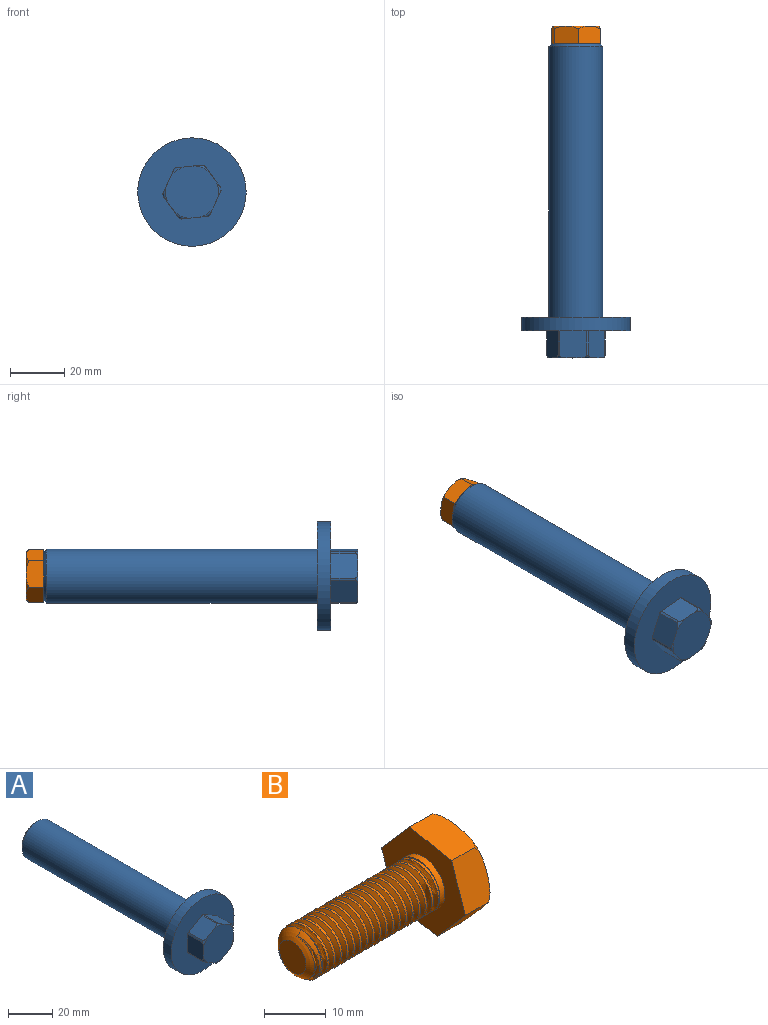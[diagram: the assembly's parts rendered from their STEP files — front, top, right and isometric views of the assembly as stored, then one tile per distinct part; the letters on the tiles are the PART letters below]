
ASSEMBLY  parts=2 mates=1
PART A: 31 faces, bbox 40x116.6x40 mm
  f0: cylinder r=4.25mm len=34.98mm, axis (0,-1,0), area 369.2mm2, adj f2,f3,f15,f29,f30
  f1: plane 17.97x17.97mm, normal (0,1,0), area 174.4mm2, adj f2,f3,f22,f30
  f2: bspline ~35.78x11.94mm, area 726mm2, adj f0,f1,f3,f29,f30
  f3: bspline ~36.03x11.94mm, area 738.2mm2, adj f0,f1,f2,f29,f30
  f4: cylinder r=10.75mm len=9mm, axis (0,-1,0), area 7.1mm2, adj f5,f19,f23,f28
  f5: torus R=9.75mm, axis (0,-1,0), area 3.7mm2, adj f4,f21,f23,f28
  f6: torus R=9.75mm, axis (0,-1,0), area 3.7mm2, adj f12,f21,f24,f28
  f7: cylinder r=10.75mm len=9mm, axis (0,-1,0), area 7.1mm2, adj f8,f19,f24,f27
  f8: torus R=9.75mm, axis (0,-1,0), area 3.7mm2, adj f7,f21,f24,f27
  f9: torus R=9.75mm, axis (0,-1,0), area 3.7mm2, adj f11,f21,f25,f27
  f10: cylinder r=10.75mm len=9mm, axis (0,-1,0), area 7.1mm2, adj f13,f19,f23,f26
  f11: cylinder r=10.75mm len=9mm, axis (0,-1,0), area 7.1mm2, adj f9,f19,f25,f27
  f12: cylinder r=10.75mm len=9mm, axis (0,-1,0), area 7.1mm2, adj f6,f19,f24,f28
  f13: torus R=9.75mm, axis (0,-1,0), area 3.7mm2, adj f10,f21,f23,f26
  f14: torus R=9.75mm, axis (0,-1,0), area 3.7mm2, adj f20,f21,f25,f26
  f15: cone r=4.25mm half-angle=45deg, axis (0,1,0), area 80.2mm2, adj f0
  f16: cylinder r=9.97mm len=100mm, axis (0,-1,0), area 6267.5mm2, adj f17,f22
  f17: plane 40x40mm, normal (0,1,0), area 944mm2, adj f16,f18
  f18: cylinder r=20mm len=40mm, axis (0,-1,0), area 628.3mm2, adj f17,f19
  f19: plane 40x40mm, normal (0,-1,0), area 944.5mm2, adj f4,f7,f10,f11,f12,f18,f20,f23
  f20: cylinder r=10.75mm len=9mm, axis (0,-1,0), area 7.1mm2, adj f14,f19,f25,f26
  f21: plane 19.5x19mm, normal (0,-1,0), area 294.2mm2, adj f5,f6,f8,f9,f13,f14,f23,f24
  f22: cone r=9.97mm half-angle=45deg, axis (0,-1,0), area 84.2mm2, adj f1,f16
  f23: plane 10x8.71mm, normal (0.5,0,0.87), area 99.6mm2, adj f4,f5,f10,f13,f19,f21
  f24: plane 10.06x10mm, normal (-1,0,0), area 99.6mm2, adj f6,f7,f8,f12,f19,f21
  f25: plane 10x8.71mm, normal (0.5,0,-0.87), area 99.6mm2, adj f9,f11,f14,f19,f20,f21
  f26: plane 10.06x10mm, normal (1,0,0), area 99.6mm2, adj f10,f13,f14,f19,f20,f21
  f27: plane 10x8.71mm, normal (-0.5,0,-0.87), area 99.6mm2, adj f7,f8,f9,f11,f19,f21
  f28: plane 10x8.71mm, normal (-0.5,0,0.87), area 99.6mm2, adj f4,f5,f6,f12,f19,f21
  f29: plane 1.06x0.8mm, normal (-0.87,0,-0.5), area 0.5mm2, adj f0,f2,f3
  f30: cone r=5.69mm half-angle=44.1deg, axis (0,1,0), area 18.1mm2, adj f0,f1,f2,f3
PART B: 17 faces, bbox 37.1x20.2x20.2 mm
  f0: plane 7.39x6.5mm, normal (0,0.75,0.66), area 60.9mm2, adj f1,f5,f6,f15
  f1: plane 9.63x6.5mm, normal (0,-0.19,0.98), area 60.9mm2, adj f0,f2,f6,f15
  f2: plane 9.29x6.5mm, normal (0,-0.95,0.32), area 60.9mm2, adj f1,f3,f6,f15
  f3: plane 7.39x6.5mm, normal (0,-0.75,-0.66), area 60.9mm2, adj f2,f4,f6,f15
  f4: plane 9.63x6.5mm, normal (0,0.19,-0.98), area 60.9mm2, adj f3,f5,f6,f15
  f5: plane 9.29x6.5mm, normal (0,0.95,-0.32), area 60.9mm2, adj f0,f4,f6,f15
  f6: plane 19.26x18.58mm, normal (-1,0,0), area 173.3mm2, adj f0,f1,f2,f3,f4,f5,f8
  f7: plane 10.43x10.43mm, normal (-1,0,0), area 11mm2, adj f8,f12,f13,f14
  f8: cylinder r=4.95mm len=9.9mm, axis (1,0,0), area 37.3mm2, adj f6,f7
  f9: plane 6.1x6.1mm, normal (-1,0,0), area 29.2mm2, adj f11
  f10: revolved ~7.92x4.55mm, area 7mm2, adj f11,f12,f13,f14
  f11: revolved ~9.68x9.68mm, area 42.9mm2, adj f9,f10,f13
  f12: bspline ~29.03x11.32mm, area 548mm2, adj f7,f10,f13,f14
  f13: bspline ~29.53x11.32mm, area 544mm2, adj f7,f10,f11,f12,f14
  f14: cylinder r=4.9mm len=27.14mm, axis (-1,0,0), area 221.9mm2, adj f7,f10,f12,f13
  f15: revolved ~19.63x19.63mm, area 36mm2, adj f0,f1,f2,f3,f4,f5,f16
  f16: plane 16.73x16.73mm, normal (1,0,0), area 219.8mm2, adj f15
PLACE A rot(axis=(0,1,0),144deg) t=(3.11,-34.8,3.6)mm
PLACE B rot(axis=(-0.3,-0.3,0.91),95.5deg) t=(3.11,-14.3,3.6)mm
MATE cylindrical B.f8 <-> A.f0  axis (0,-1,0) through (3.11,15.7,3.6)mm
